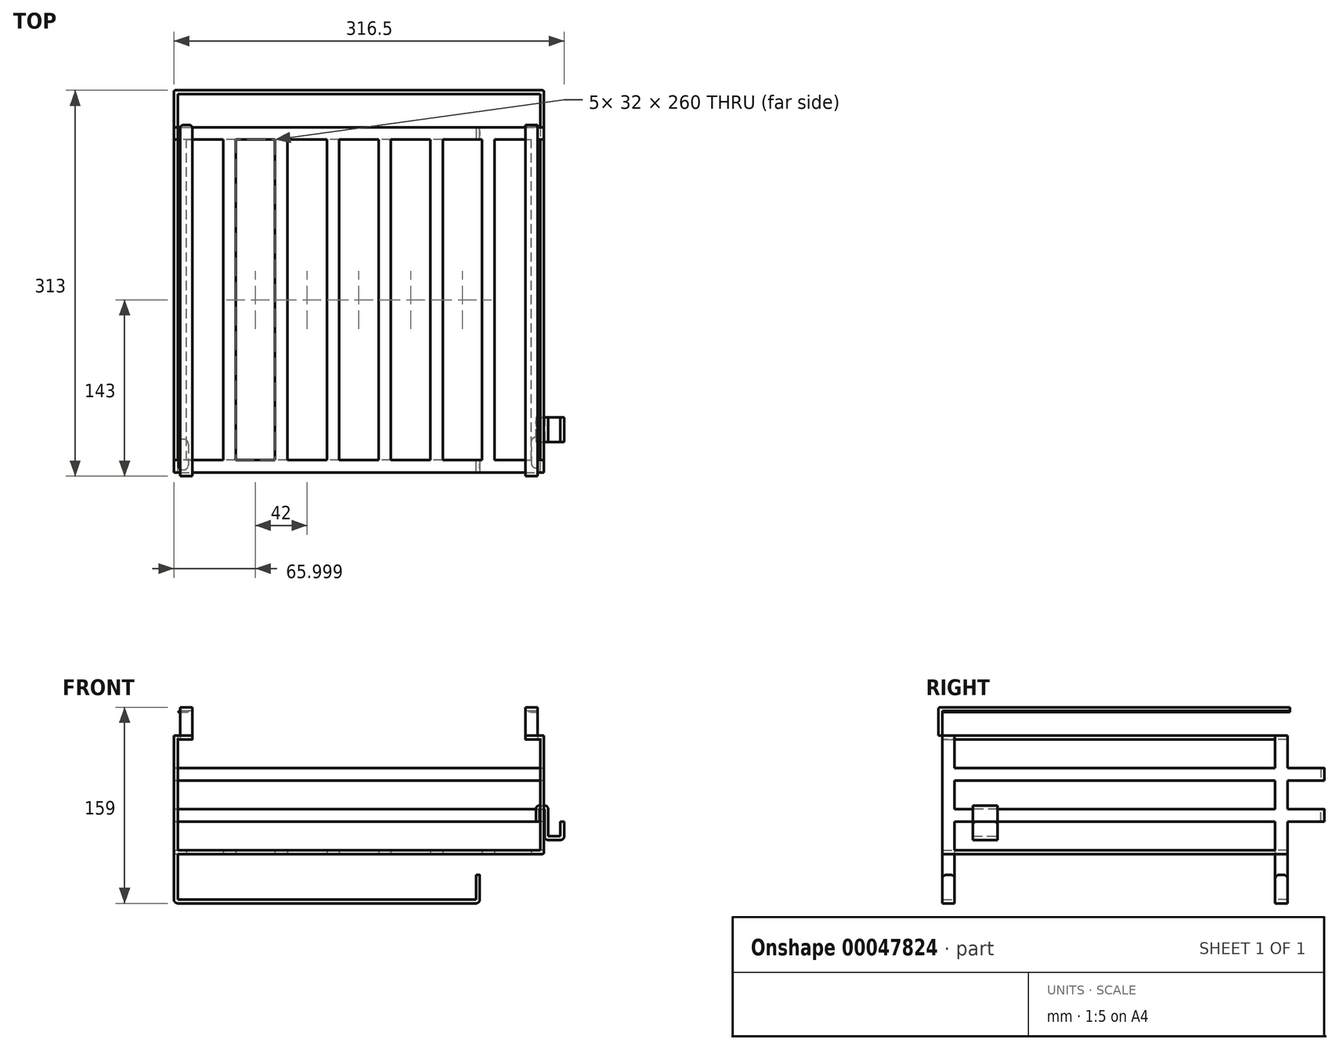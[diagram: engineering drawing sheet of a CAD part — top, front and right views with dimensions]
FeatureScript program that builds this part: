
annotation { "Feature Type Name" : "Feature", "Feature Type Description" : "" }
export const myFeature = defineFeature(function(context is Context, id is Id, definition is map)
    precondition{}
    {
        {
            var Q0;
            Q0=qCreatedBy(makeId("Top.planeOp"),FACE);
            var sketch = newSketch(context, id + "F0", { "sketchPlane" : qUnion([Q0])});
            skLineSegment(sketch, "E0.bottom", {"start": v(-155.28, 215.65) * mm, "end": v(144.72, 215.65) * mm});
            skLineSegment(sketch, "E0.top", {"start": v(-155.28, -94.35) * mm, "end": v(144.72, -94.35) * mm});
            skLineSegment(sketch, "E0.left", {"start": v(-155.28, 215.65) * mm, "end": v(-155.28, -94.35) * mm});
            skLineSegment(sketch, "E0.right", {"start": v(144.72, 215.65) * mm, "end": v(144.72, -94.35) * mm});
            skLineSegment(sketch, "E1", {"start": v(-155.28, -84.35) * mm, "end": v(144.72, -84.35) * mm});
            skLineSegment(sketch, "E2", {"start": v(-115.28, -84.35) * mm, "end": v(-115.28, 175.65) * mm});
            skLineSegment(sketch, "E3.0", {"start": v(-105.28, -84.35) * mm, "end": v(-105.28, 175.65) * mm});
            skLineSegment(sketch, "E4", {"start": v(-73.28, -84.35) * mm, "end": v(-73.28, 175.65) * mm});
            skLineSegment(sketch, "E5.0", {"start": v(-63.28, -84.35) * mm, "end": v(-63.28, 175.65) * mm});
            skLineSegment(sketch, "E6.0", {"start": v(-31.28, -84.35) * mm, "end": v(-31.28, 175.65) * mm});
            skLineSegment(sketch, "E7.0", {"start": v(-21.28, -84.35) * mm, "end": v(-21.28, 175.65) * mm});
            skLineSegment(sketch, "E8.0", {"start": v(10.72, -84.35) * mm, "end": v(10.72, 175.65) * mm});
            skLineSegment(sketch, "E9.0", {"start": v(20.72, -84.35) * mm, "end": v(20.72, 175.65) * mm});
            skLineSegment(sketch, "E10.0", {"start": v(52.72, -84.35) * mm, "end": v(52.72, 175.65) * mm});
            skLineSegment(sketch, "E11.0", {"start": v(62.72, -84.35) * mm, "end": v(62.72, 175.65) * mm});
            skLineSegment(sketch, "E12.0", {"start": v(94.72, -84.35) * mm, "end": v(94.72, 175.65) * mm});
            skLineSegment(sketch, "E13.0", {"start": v(104.72, -84.35) * mm, "end": v(104.72, 175.65) * mm});
            skLineSegment(sketch, "E14", {"start": v(-115.28, -42.82) * mm, "end": v(-155.28, -42.82) * mm, "construction": true});
            skLineSegment(sketch, "E15", {"start": v(104.72, -42.82) * mm, "end": v(144.72, -42.82) * mm, "construction": true});
            skLineSegment(sketch, "E16", {"start": v(-155.28, 175.65) * mm, "end": v(144.72, 175.65) * mm});
            skLineSegment(sketch, "E17.0", {"start": v(-155.28, 185.65) * mm, "end": v(144.72, 185.65) * mm});
            skLineSegment(sketch, "E18", {"start": v(-145.28, -84.35) * mm, "end": v(-145.28, 175.65) * mm});
            skLineSegment(sketch, "E19", {"start": v(134.72, -84.35) * mm, "end": v(134.72, 175.65) * mm});
            skSolve(sketch);
        }
        {
            var Q0;
            {var subQ13=sQuery(id+"F0.wireOp",EDGE,"E17.0");Q0=makeQuery(id+"F0.imprint","IMPRINT",FACE,{"disambiguationData":[TD([[makeQuery(id+"F0.imprint","IMPRINT",EDGE,{"derivedFrom":subQ13}),-1.0]])]});}
            var Q1;
            {var subQ2=sQuery(id+"F0.wireOp",EDGE,"E2");Q1=makeQuery(id+"F0.imprint","IMPRINT",FACE,{"disambiguationData":[TD([[makeQuery(id+"F0.imprint","IMPRINT",EDGE,{"derivedFrom":subQ2}),-1.0]])]});}
            var Q2;
            {var subQ2=sQuery(id+"F0.wireOp",EDGE,"E4");Q2=makeQuery(id+"F0.imprint","IMPRINT",FACE,{"disambiguationData":[TD([[makeQuery(id+"F0.imprint","IMPRINT",EDGE,{"derivedFrom":subQ2}),-1.0]])]});}
            var Q3;
            {var subQ2=sQuery(id+"F0.wireOp",EDGE,"E6.0");Q3=makeQuery(id+"F0.imprint","IMPRINT",FACE,{"disambiguationData":[TD([[makeQuery(id+"F0.imprint","IMPRINT",EDGE,{"derivedFrom":subQ2}),-1.0]])]});}
            var Q4;
            {var subQ2=sQuery(id+"F0.wireOp",EDGE,"E8.0");Q4=makeQuery(id+"F0.imprint","IMPRINT",FACE,{"disambiguationData":[TD([[makeQuery(id+"F0.imprint","IMPRINT",EDGE,{"derivedFrom":subQ2}),-1.0]])]});}
            var Q5;
            {var subQ2=sQuery(id+"F0.wireOp",EDGE,"E10.0");Q5=makeQuery(id+"F0.imprint","IMPRINT",FACE,{"disambiguationData":[TD([[makeQuery(id+"F0.imprint","IMPRINT",EDGE,{"derivedFrom":subQ2}),-1.0]])]});}
            var Q6;
            {var subQ2=sQuery(id+"F0.wireOp",EDGE,"E12.0");Q6=makeQuery(id+"F0.imprint","IMPRINT",FACE,{"disambiguationData":[TD([[makeQuery(id+"F0.imprint","IMPRINT",EDGE,{"derivedFrom":subQ2}),-1.0]])]});}
            var Q7;
            {var subQ6=sQuery(id+"F0.wireOp",EDGE,"E0.top");Q7=makeQuery(id+"F0.imprint","IMPRINT",FACE,{"disambiguationData":[TD([[makeQuery(id+"F0.imprint","IMPRINT",EDGE,{"derivedFrom":subQ6}),1.0]])]});}
            var Q8;
            {var subQ0=sQuery(id+"F0.wireOp",EDGE,"E18");Q8=makeQuery(id+"F0.imprint","IMPRINT",FACE,{"disambiguationData":[TD([[makeQuery(id+"F0.imprint","IMPRINT",EDGE,{"derivedFrom":subQ0}),1.0]])]});}
            var Q9;
            {var subQ0=sQuery(id+"F0.wireOp",EDGE,"E19");Q9=makeQuery(id+"F0.imprint","IMPRINT",FACE,{"disambiguationData":[TD([[makeQuery(id+"F0.imprint","IMPRINT",EDGE,{"derivedFrom":subQ0}),-1.0]])]});}
            extrude(context, id + "F1", {"entities" : qUnion([Q0, Q1, Q2, Q3, Q4, Q5, Q6, Q7, Q8, Q9]), "depth" : 3 * mm});
        }
        {
            var Q0;
            Q0=makeQuery(id+"F1.opExtrude","CAP_FACE",FACE,{"disambiguationData":[OSD([sQuery(id+"F0.wireOp",EDGE,"E0.top"),sQuery(id+"F0.wireOp",EDGE,"E0.left"),sQuery(id+"F0.wireOp",EDGE,"E0.right"),sQuery(id+"F0.wireOp",EDGE,"E1"),sQuery(id+"F0.wireOp",EDGE,"E2"),sQuery(id+"F0.wireOp",EDGE,"E3.0"),sQuery(id+"F0.wireOp",EDGE,"E4"),sQuery(id+"F0.wireOp",EDGE,"E5.0"),sQuery(id+"F0.wireOp",EDGE,"E6.0"),sQuery(id+"F0.wireOp",EDGE,"E7.0"),sQuery(id+"F0.wireOp",EDGE,"E8.0"),sQuery(id+"F0.wireOp",EDGE,"E9.0"),sQuery(id+"F0.wireOp",EDGE,"E10.0"),sQuery(id+"F0.wireOp",EDGE,"E11.0"),sQuery(id+"F0.wireOp",EDGE,"E12.0"),sQuery(id+"F0.wireOp",EDGE,"E13.0"),sQuery(id+"F0.wireOp",EDGE,"E16"),sQuery(id+"F0.wireOp",EDGE,"E17.0")])],"isStart":false});
            var sketch = newSketch(context, id + "F2", { "sketchPlane" : qUnion([Q0])});
            skLineSegment(sketch, "E20.bottom", {"start": v(-155.28, 185.65) * mm, "end": v(-152.28, 185.65) * mm});
            skLineSegment(sketch, "E20.top", {"start": v(-155.28, 175.65) * mm, "end": v(-152.28, 175.65) * mm});
            skLineSegment(sketch, "E20.left", {"start": v(-155.28, 185.65) * mm, "end": v(-155.28, 175.65) * mm});
            skLineSegment(sketch, "E20.right", {"start": v(-152.28, 185.65) * mm, "end": v(-152.28, 175.65) * mm});
            skLineSegment(sketch, "E21.bottom", {"start": v(-155.28, -94.35) * mm, "end": v(-152.28, -94.35) * mm});
            skLineSegment(sketch, "E21.top", {"start": v(-155.28, -84.35) * mm, "end": v(-152.28, -84.35) * mm});
            skLineSegment(sketch, "E21.left", {"start": v(-155.28, -94.35) * mm, "end": v(-155.28, -84.35) * mm});
            skLineSegment(sketch, "E21.right", {"start": v(-152.28, -94.35) * mm, "end": v(-152.28, -84.35) * mm});
            skLineSegment(sketch, "E22", {"start": v(-5.28, 152.07) * mm, "end": v(-5.28, 185.65) * mm, "construction": true});
            skLineSegment(sketch, "E23.MirrorCS", {"start": v(141.72, 185.65) * mm, "end": v(141.72, 175.65) * mm});
            skLineSegment(sketch, "E24.MirrorCS", {"start": v(144.72, 185.65) * mm, "end": v(144.72, 175.65) * mm});
            skLineSegment(sketch, "E25.MirrorCS", {"start": v(144.72, 185.65) * mm, "end": v(141.72, 185.65) * mm});
            skLineSegment(sketch, "E26.MirrorCS", {"start": v(144.72, 175.65) * mm, "end": v(141.72, 175.65) * mm});
            skLineSegment(sketch, "E27.MirrorCS", {"start": v(141.72, -94.35) * mm, "end": v(141.72, -84.35) * mm});
            skLineSegment(sketch, "E28.MirrorCS", {"start": v(144.72, -94.35) * mm, "end": v(144.72, -84.35) * mm});
            skLineSegment(sketch, "E29.MirrorCS", {"start": v(144.72, -84.35) * mm, "end": v(141.72, -84.35) * mm});
            skLineSegment(sketch, "E30.MirrorCS", {"start": v(144.72, -94.35) * mm, "end": v(141.72, -94.35) * mm});
            skSolve(sketch);
        }
        {
            var Q0;
            Q0=makeQuery(id+"F2.imprint","IMPRINT",FACE,{"disambiguationData":[TD([[makeQuery(id+"F2.imprint","IMPRINT",EDGE,{"derivedFrom":sQuery(id+"F2.wireOp",EDGE,"E20.bottom")}),-1.0]])]});
            var Q1;
            Q1=makeQuery(id+"F2.imprint","IMPRINT",FACE,{"disambiguationData":[TD([[makeQuery(id+"F2.imprint","IMPRINT",EDGE,{"derivedFrom":sQuery(id+"F2.wireOp",EDGE,"E23.MirrorCS")}),1.0]])]});
            var Q2;
            Q2=makeQuery(id+"F2.imprint","IMPRINT",FACE,{"disambiguationData":[TD([[makeQuery(id+"F2.imprint","IMPRINT",EDGE,{"derivedFrom":sQuery(id+"F2.wireOp",EDGE,"E27.MirrorCS")}),-1.0]])]});
            var Q3;
            Q3=makeQuery(id+"F2.imprint","IMPRINT",FACE,{"disambiguationData":[TD([[makeQuery(id+"F2.imprint","IMPRINT",EDGE,{"derivedFrom":sQuery(id+"F2.wireOp",EDGE,"E21.bottom")}),1.0]])]});
            extrude(context, id + "F3", {"entities" : qUnion([Q0, Q1, Q2, Q3]), "operationType" : NewBodyOperationType.ADD, "depth" : 90 * mm});
        }
        {
            var Q0;
            Q0=makeQuery(id+"F3.opExtrude","CAP_FACE",FACE,{"disambiguationData":[OSD([sQuery(id+"F2.wireOp",EDGE,"E20.bottom"),sQuery(id+"F2.wireOp",EDGE,"E20.top"),sQuery(id+"F2.wireOp",EDGE,"E20.left"),sQuery(id+"F2.wireOp",EDGE,"E20.right")])],"isStart":false});
            var sketch = newSketch(context, id + "F4", { "sketchPlane" : qUnion([Q0])});
            skLineSegment(sketch, "E31.bottom", {"start": v(-150.28, 185.65) * mm, "end": v(-140.28, 185.65) * mm});
            skLineSegment(sketch, "E31.top", {"start": v(-150.28, -94.35) * mm, "end": v(-140.28, -94.35) * mm});
            skLineSegment(sketch, "E31.left", {"start": v(-150.28, 185.65) * mm, "end": v(-150.28, -94.35) * mm});
            skLineSegment(sketch, "E31.right", {"start": v(-140.28, 185.65) * mm, "end": v(-140.28, -94.35) * mm});
            skLineSegment(sketch, "E32.MirrorCS", {"start": v(129.72, 185.65) * mm, "end": v(129.72, -94.35) * mm});
            skLineSegment(sketch, "E33.MirrorCS", {"start": v(139.72, 185.65) * mm, "end": v(139.72, -94.35) * mm});
            skLineSegment(sketch, "E34.MirrorCS", {"start": v(139.72, 185.65) * mm, "end": v(129.72, 185.65) * mm});
            skLineSegment(sketch, "E35.MirrorCS", {"start": v(139.72, -94.35) * mm, "end": v(129.72, -94.35) * mm});
            skLineSegment(sketch, "E36.bottom", {"start": v(-150.28, -94.35) * mm, "end": v(-155.28, -94.35) * mm});
            skLineSegment(sketch, "E36.top", {"start": v(-150.28, -84.35) * mm, "end": v(-155.28, -84.35) * mm});
            skLineSegment(sketch, "E36.left", {"start": v(-150.28, -94.35) * mm, "end": v(-150.28, -84.35) * mm});
            skLineSegment(sketch, "E36.right", {"start": v(-155.28, -94.35) * mm, "end": v(-155.28, -84.35) * mm});
            skLineSegment(sketch, "E37.MirrorCS", {"start": v(139.72, -84.35) * mm, "end": v(144.72, -84.35) * mm});
            skLineSegment(sketch, "E38.MirrorCS", {"start": v(144.72, -94.35) * mm, "end": v(144.72, -84.35) * mm});
            skLineSegment(sketch, "E39.MirrorCS", {"start": v(139.72, -94.35) * mm, "end": v(144.72, -94.35) * mm});
            skLineSegment(sketch, "E40.bottom", {"start": v(-150.28, 185.65) * mm, "end": v(-155.28, 185.65) * mm});
            skLineSegment(sketch, "E40.top", {"start": v(-150.28, 175.65) * mm, "end": v(-155.28, 175.65) * mm});
            skLineSegment(sketch, "E40.left", {"start": v(-150.28, 185.65) * mm, "end": v(-150.28, 175.65) * mm});
            skLineSegment(sketch, "E40.right", {"start": v(-155.28, 185.65) * mm, "end": v(-155.28, 175.65) * mm});
            skLineSegment(sketch, "E41.MirrorCS", {"start": v(139.72, 175.65) * mm, "end": v(144.72, 175.65) * mm});
            skLineSegment(sketch, "E42.MirrorCS", {"start": v(139.72, 185.65) * mm, "end": v(144.72, 185.65) * mm});
            skLineSegment(sketch, "E43.MirrorCS", {"start": v(144.72, 185.65) * mm, "end": v(144.72, 175.65) * mm});
            skLineSegment(sketch, "E44.bottom", {"start": v(-140.28, -94.35) * mm, "end": v(-150.28, -94.35) * mm});
            skLineSegment(sketch, "E44.top", {"start": v(-140.28, -97.35) * mm, "end": v(-150.28, -97.35) * mm});
            skLineSegment(sketch, "E44.left", {"start": v(-140.28, -94.35) * mm, "end": v(-140.28, -97.35) * mm});
            skLineSegment(sketch, "E44.right", {"start": v(-150.28, -94.35) * mm, "end": v(-150.28, -97.35) * mm});
            skLineSegment(sketch, "E45.top", {"start": v(139.72, -97.35) * mm, "end": v(129.72, -97.35) * mm});
            skLineSegment(sketch, "E45.left", {"start": v(139.72, -94.35) * mm, "end": v(139.72, -97.35) * mm});
            skLineSegment(sketch, "E45.right", {"start": v(129.72, -94.35) * mm, "end": v(129.72, -97.35) * mm});
            skSolve(sketch);
        }
        {
            var Q0;
            Q0=makeQuery(id+"F4.imprint","IMPRINT",FACE,{"disambiguationData":[TD([[makeQuery(id+"F4.imprint","IMPRINT",EDGE,{"derivedFrom":sQuery(id+"F4.wireOp",EDGE,"E31.bottom")}),-1.0]])]});
            var Q1;
            {var subQ1=sQuery(id+"F4.wireOp",EDGE,"E40.left");Q1=makeQuery(id+"F4.imprint","IMPRINT",FACE,{"disambiguationData":[TD([[makeQuery(id+"F4.imprint","IMPRINT",EDGE,{"derivedFrom":subQ1}),-1.0]])]});}
            var Q2;
            {var subQ1=sQuery(id+"F4.wireOp",EDGE,"E40.right");Q2=makeQuery(id+"F4.imprint","IMPRINT",FACE,{"disambiguationData":[TD([[makeQuery(id+"F4.imprint","IMPRINT",EDGE,{"derivedFrom":subQ1}),1.0]])]});}
            var Q3;
            Q3=makeQuery(id+"F4.imprint","IMPRINT",FACE,{"disambiguationData":[TD([[makeQuery(id+"F4.imprint","IMPRINT",EDGE,{"derivedFrom":sQuery(id+"F4.wireOp",EDGE,"E44.bottom")}),1.0]])]});
            var Q4;
            Q4=makeQuery(id+"F4.imprint","IMPRINT",FACE,{"disambiguationData":[TD([[makeQuery(id+"F4.imprint","IMPRINT",EDGE,{"derivedFrom":sQuery(id+"F4.wireOp",EDGE,"E35.MirrorCS")}),1.0]])]});
            var Q5;
            Q5=makeQuery(id+"F4.imprint","IMPRINT",FACE,{"disambiguationData":[TD([[makeQuery(id+"F4.imprint","IMPRINT",EDGE,{"derivedFrom":sQuery(id+"F4.wireOp",EDGE,"E32.MirrorCS")}),1.0]])]});
            var Q6;
            {var subQ1=sQuery(id+"F4.wireOp",EDGE,"E37.MirrorCS");Q6=makeQuery(id+"F4.imprint","IMPRINT",FACE,{"disambiguationData":[TD([[makeQuery(id+"F4.imprint","IMPRINT",EDGE,{"derivedFrom":subQ1}),-1.0]])]});}
            var Q7;
            {var subQ1=sQuery(id+"F4.wireOp",EDGE,"E41.MirrorCS");Q7=makeQuery(id+"F4.imprint","IMPRINT",FACE,{"disambiguationData":[TD([[makeQuery(id+"F4.imprint","IMPRINT",EDGE,{"derivedFrom":subQ1}),1.0]])]});}
            var Q8;
            Q8=makeQuery(id+"F4.imprint","IMPRINT",FACE,{"disambiguationData":[TD([[makeQuery(id+"F4.imprint","IMPRINT",EDGE,{"derivedFrom":sQuery(id+"F4.wireOp",EDGE,"E36.bottom")}),-1.0]])]});
            extrude(context, id + "F5", {"entities" : qUnion([Q0, Q1, Q2, Q3, Q4, Q5, Q6, Q7, Q8]), "operationType" : NewBodyOperationType.ADD, "depth" : 3 * mm});
        }
        {
            var Q0;
            Q0=makeQuery(id+"F5.opExtrude","CAP_FACE",FACE,{"disambiguationData":[OSD([sQuery(id+"F4.wireOp",EDGE,"E31.bottom"),sQuery(id+"F4.wireOp",EDGE,"E31.top"),sQuery(id+"F4.wireOp",EDGE,"E31.left"),sQuery(id+"F4.wireOp",EDGE,"E31.right")])],"isStart":false});
            var sketch = newSketch(context, id + "F6", { "sketchPlane" : qUnion([Q0])});
            skLineSegment(sketch, "E46.bottom", {"start": v(-140.28, -97.35) * mm, "end": v(-150.28, -97.35) * mm});
            skLineSegment(sketch, "E46.top", {"start": v(-140.28, -94.35) * mm, "end": v(-150.28, -94.35) * mm});
            skLineSegment(sketch, "E46.left", {"start": v(-140.28, -97.35) * mm, "end": v(-140.28, -94.35) * mm});
            skLineSegment(sketch, "E46.right", {"start": v(-150.28, -97.35) * mm, "end": v(-150.28, -94.35) * mm});
            skLineSegment(sketch, "E47.MirrorCS", {"start": v(129.72, -94.35) * mm, "end": v(139.72, -94.35) * mm});
            skLineSegment(sketch, "E48.MirrorCS", {"start": v(139.72, -97.35) * mm, "end": v(139.72, -94.35) * mm});
            skLineSegment(sketch, "E49.MirrorCS", {"start": v(129.72, -97.35) * mm, "end": v(129.72, -94.35) * mm});
            skLineSegment(sketch, "E50.MirrorCS", {"start": v(129.72, -97.35) * mm, "end": v(139.72, -97.35) * mm});
            skSolve(sketch);
        }
        {
            var Q0;
            Q0=makeQuery(id+"F6.imprint","IMPRINT",FACE,{"disambiguationData":[TD([[makeQuery(id+"F6.imprint","IMPRINT",EDGE,{"derivedFrom":sQuery(id+"F6.wireOp",EDGE,"E46.bottom")}),-1.0]])]});
            var Q1;
            Q1=makeQuery(id+"F6.imprint","IMPRINT",FACE,{"disambiguationData":[TD([[makeQuery(id+"F6.imprint","IMPRINT",EDGE,{"derivedFrom":sQuery(id+"F6.wireOp",EDGE,"E47.MirrorCS")}),-1.0]])]});
            extrude(context, id + "F7", {"entities" : qUnion([Q0, Q1]), "operationType" : NewBodyOperationType.ADD, "depth" : 20 * mm});
        }
        {
            var Q0;
            Q0=makeQuery(id+"F7.opExtrude","CAP_FACE",FACE,{"disambiguationData":[OSD([sQuery(id+"F6.wireOp",EDGE,"E46.bottom"),sQuery(id+"F6.wireOp",EDGE,"E46.top"),sQuery(id+"F6.wireOp",EDGE,"E46.left"),sQuery(id+"F6.wireOp",EDGE,"E46.right")])],"isStart":false});
            var sketch = newSketch(context, id + "F8", { "sketchPlane" : qUnion([Q0])});
            skLineSegment(sketch, "E51.bottom", {"start": v(-150.28, -97.35) * mm, "end": v(-140.28, -97.35) * mm});
            skLineSegment(sketch, "E51.top", {"start": v(-150.28, 187.65) * mm, "end": v(-140.28, 187.65) * mm});
            skLineSegment(sketch, "E51.left", {"start": v(-150.28, -97.35) * mm, "end": v(-150.28, 187.65) * mm});
            skLineSegment(sketch, "E51.right", {"start": v(-140.28, -97.35) * mm, "end": v(-140.28, 187.65) * mm});
            skLineSegment(sketch, "E52.MirrorCS", {"start": v(129.72, -97.35) * mm, "end": v(129.72, 187.65) * mm});
            skLineSegment(sketch, "E53.MirrorCS", {"start": v(139.72, 187.65) * mm, "end": v(129.72, 187.65) * mm});
            skLineSegment(sketch, "E54.MirrorCS", {"start": v(139.72, -97.35) * mm, "end": v(139.72, 187.65) * mm});
            skLineSegment(sketch, "E55.MirrorCS", {"start": v(139.72, -97.35) * mm, "end": v(129.72, -97.35) * mm});
            skPoint(sketch, "E56", {"position": v(-140.28, 45.15) * mm});
            skSolve(sketch);
        }
        {
            var Q0;
            {var subQ1=sQuery(id+"F8.wireOp",EDGE,"E51.top");Q0=makeQuery(id+"F8.imprint","IMPRINT",FACE,{"disambiguationData":[TD([[makeQuery(id+"F8.imprint","IMPRINT",EDGE,{"derivedFrom":subQ1}),-1.0]])]});}
            var Q1;
            Q1=makeQuery(id+"F8.imprint","IMPRINT",FACE,{"disambiguationData":[TD([[makeQuery(id+"F8.imprint","IMPRINT",EDGE,{"derivedFrom":sQuery(id+"F8.wireOp",EDGE,"E52.MirrorCS")}),-1.0]])]});
            var Q2;
            {var subQ2=sQuery(id+"F8.wireOp",EDGE,"E51.bottom");Q2=makeQuery(id+"F8.imprint","IMPRINT",FACE,{"disambiguationData":[TD([[makeQuery(id+"F8.imprint","IMPRINT",EDGE,{"derivedFrom":subQ2}),1.0]])]});}
            var Q3;
            {var subQ2=sQuery(id+"F8.wireOp",EDGE,"E51.bottom");Q3=makeQuery(id+"F8.imprint","IMPRINT",FACE,{"disambiguationData":[TD([[makeQuery(id+"F8.imprint","IMPRINT",EDGE,{"derivedFrom":subQ2}),-1.0]])]});}
            extrude(context, id + "F9", {"entities" : qUnion([Q0, Q1, Q2, Q3]), "operationType" : NewBodyOperationType.ADD, "depth" : 3 * mm});
        }
        {
            var Q0;
            Q0=makeQuery(id+"F5.boolean.opBoolean","MERGE",FACE,{"derivedFrom":[makeQuery(id+"F3.boolean.opBoolean","MERGE",FACE,{"derivedFrom":[makeQuery(id+"F1.opExtrude","SWEPT_FACE",FACE,{"disambiguationData":[OSD([sQuery(id+"F0.wireOp",EDGE,"E17.0")])]}),makeQuery(id+"F3.opExtrude","SWEPT_FACE",FACE,{"disambiguationData":[OSD([sQuery(id+"F2.wireOp",EDGE,"E20.bottom")])]}),makeQuery(id+"F3.opExtrude","SWEPT_FACE",FACE,{"disambiguationData":[OSD([sQuery(id+"F2.wireOp",EDGE,"E25.MirrorCS")])]})]}),makeQuery(id+"F5.opExtrude","SWEPT_FACE",FACE,{"disambiguationData":[OSD([sQuery(id+"F4.wireOp",EDGE,"E31.bottom")])]}),makeQuery(id+"F5.opExtrude","SWEPT_FACE",FACE,{"disambiguationData":[OSD([sQuery(id+"F4.wireOp",EDGE,"E34.MirrorCS")])]})]});
            var sketch = newSketch(context, id + "F10", { "sketchPlane" : qUnion([Q0])});
            skLineSegment(sketch, "E57", {"start": v(152.28, 3) * mm, "end": v(155.28, 3) * mm, "construction": true});
            skLineSegment(sketch, "E58", {"start": v(152.28, 93) * mm, "end": v(155.28, 93) * mm, "construction": true});
            skLineSegment(sketch, "E59.bottom", {"start": v(155.28, 69.67) * mm, "end": v(152.28, 69.67) * mm});
            skLineSegment(sketch, "E59.top", {"start": v(155.28, 59.67) * mm, "end": v(152.28, 59.67) * mm});
            skLineSegment(sketch, "E59.left", {"start": v(155.28, 69.67) * mm, "end": v(155.28, 59.67) * mm});
            skLineSegment(sketch, "E59.right", {"start": v(152.28, 69.67) * mm, "end": v(152.28, 59.67) * mm});
            skLineSegment(sketch, "E60.bottom", {"start": v(155.28, 36.33) * mm, "end": v(152.28, 36.33) * mm});
            skLineSegment(sketch, "E60.top", {"start": v(155.28, 26.33) * mm, "end": v(152.28, 26.33) * mm});
            skLineSegment(sketch, "E60.left", {"start": v(155.28, 36.33) * mm, "end": v(155.28, 26.33) * mm});
            skLineSegment(sketch, "E60.right", {"start": v(152.28, 36.33) * mm, "end": v(152.28, 26.33) * mm});
            skLineSegment(sketch, "E61", {"start": v(153.78, 93) * mm, "end": v(153.78, 69.67) * mm, "construction": true});
            skLineSegment(sketch, "E62", {"start": v(153.78, 59.67) * mm, "end": v(153.78, 36.33) * mm, "construction": true});
            skLineSegment(sketch, "E63", {"start": v(153.78, 26.33) * mm, "end": v(153.78, 3) * mm, "construction": true});
            skLineSegment(sketch, "E64", {"start": v(5.28, 3) * mm, "end": v(5.28, 25.42) * mm, "construction": true});
            skLineSegment(sketch, "E65.MirrorCS", {"start": v(-144.72, 26.33) * mm, "end": v(-141.72, 26.33) * mm});
            skLineSegment(sketch, "E66.MirrorCS", {"start": v(-144.72, 36.33) * mm, "end": v(-141.72, 36.33) * mm});
            skLineSegment(sketch, "E67.MirrorCS", {"start": v(-141.72, 36.33) * mm, "end": v(-141.72, 26.33) * mm});
            skLineSegment(sketch, "E68.MirrorCS", {"start": v(-144.72, 36.33) * mm, "end": v(-144.72, 26.33) * mm});
            skLineSegment(sketch, "E69.MirrorCS", {"start": v(-144.72, 59.67) * mm, "end": v(-141.72, 59.67) * mm});
            skLineSegment(sketch, "E70.MirrorCS", {"start": v(-141.72, 69.67) * mm, "end": v(-141.72, 59.67) * mm});
            skLineSegment(sketch, "E71.MirrorCS", {"start": v(-144.72, 69.67) * mm, "end": v(-144.72, 59.67) * mm});
            skLineSegment(sketch, "E72.MirrorCS", {"start": v(-144.72, 69.67) * mm, "end": v(-141.72, 69.67) * mm});
            skSolve(sketch);
        }
        {
            var Q0;
            Q0=makeQuery(id+"F10.imprint","IMPRINT",FACE,{"disambiguationData":[TD([[makeQuery(id+"F10.imprint","IMPRINT",EDGE,{"derivedFrom":sQuery(id+"F10.wireOp",EDGE,"E59.bottom")}),1.0]])]});
            var Q1;
            Q1=makeQuery(id+"F10.imprint","IMPRINT",FACE,{"disambiguationData":[TD([[makeQuery(id+"F10.imprint","IMPRINT",EDGE,{"derivedFrom":sQuery(id+"F10.wireOp",EDGE,"E60.bottom")}),1.0]])]});
            var Q2;
            Q2=makeQuery(id+"F10.imprint","IMPRINT",FACE,{"disambiguationData":[TD([[makeQuery(id+"F10.imprint","IMPRINT",EDGE,{"derivedFrom":sQuery(id+"F10.wireOp",EDGE,"E69.MirrorCS")}),1.0]])]});
            var Q3;
            Q3=makeQuery(id+"F10.imprint","IMPRINT",FACE,{"disambiguationData":[TD([[makeQuery(id+"F10.imprint","IMPRINT",EDGE,{"derivedFrom":sQuery(id+"F10.wireOp",EDGE,"E65.MirrorCS")}),1.0]])]});
            var Q4;
            Q4=makeQuery(id+"F5.boolean.opBoolean","MERGE",FACE,{"derivedFrom":[makeQuery(id+"F3.opExtrude","SWEPT_FACE",FACE,{"disambiguationData":[OSD([sQuery(id+"F2.wireOp",EDGE,"E21.top")])]}),makeQuery(id+"F5.opExtrude","SWEPT_FACE",FACE,{"disambiguationData":[OSD([sQuery(id+"F4.wireOp",EDGE,"E36.top")])]})]});
            extrude(context, id + "F11", {"entities" : qUnion([Q0, Q1, Q2, Q3]), "operationType" : NewBodyOperationType.ADD, "depth" : 30 * mm, "hasSecondDirection" : true, "secondDirectionBound" : SecondDirectionBoundingType.UP_TO_SURFACE, "secondDirectionOppositeDirection" : true, "secondDirectionBoundEntityFace" : qUnion([Q4]), "secondDirectionDepth" : 25 * mm});
        }
        {
            var Q0;
            Q0=makeQuery(id+"F11.boolean.opBoolean","MERGE",FACE,{"derivedFrom":[makeQuery(id+"F3.opExtrude","SWEPT_FACE",FACE,{"disambiguationData":[OSD([sQuery(id+"F2.wireOp",EDGE,"E20.right")])]}),makeQuery(id+"F3.opExtrude","SWEPT_FACE",FACE,{"disambiguationData":[OSD([sQuery(id+"F2.wireOp",EDGE,"E21.right")])]}),makeQuery(id+"F11.opExtrude","SWEPT_FACE",FACE,{"disambiguationData":[OSD([sQuery(id+"F10.wireOp",EDGE,"E59.right")])]}),makeQuery(id+"F11.opExtrude","SWEPT_FACE",FACE,{"disambiguationData":[OSD([sQuery(id+"F10.wireOp",EDGE,"E60.right")])]})]});
            var sketch = newSketch(context, id + "F12", { "sketchPlane" : qUnion([Q0])});
            skLineSegment(sketch, "E73.bottom", {"start": v(215.65, 69.67) * mm, "end": v(212.65, 69.67) * mm});
            skLineSegment(sketch, "E73.top", {"start": v(215.65, 59.67) * mm, "end": v(212.65, 59.67) * mm});
            skLineSegment(sketch, "E73.left", {"start": v(215.65, 69.67) * mm, "end": v(215.65, 59.67) * mm});
            skLineSegment(sketch, "E73.right", {"start": v(212.65, 69.67) * mm, "end": v(212.65, 59.67) * mm});
            skLineSegment(sketch, "E74.bottom", {"start": v(215.65, 26.33) * mm, "end": v(212.65, 26.33) * mm});
            skLineSegment(sketch, "E74.top", {"start": v(215.65, 36.33) * mm, "end": v(212.65, 36.33) * mm});
            skLineSegment(sketch, "E74.left", {"start": v(215.65, 26.33) * mm, "end": v(215.65, 36.33) * mm});
            skLineSegment(sketch, "E74.right", {"start": v(212.65, 26.33) * mm, "end": v(212.65, 36.33) * mm});
            skSolve(sketch);
        }
        {
            var Q0;
            Q0=makeQuery(id+"F12.imprint","IMPRINT",FACE,{"disambiguationData":[TD([[makeQuery(id+"F12.imprint","IMPRINT",EDGE,{"derivedFrom":sQuery(id+"F12.wireOp",EDGE,"E73.bottom")}),1.0]])]});
            var Q1;
            Q1=makeQuery(id+"F12.imprint","IMPRINT",FACE,{"disambiguationData":[TD([[makeQuery(id+"F12.imprint","IMPRINT",EDGE,{"derivedFrom":sQuery(id+"F12.wireOp",EDGE,"E74.bottom")}),-1.0]])]});
            var Q2;
            Q2=makeQuery(id+"F11.boolean.opBoolean","MERGE",FACE,{"derivedFrom":[makeQuery(id+"F3.opExtrude","SWEPT_FACE",FACE,{"disambiguationData":[OSD([sQuery(id+"F2.wireOp",EDGE,"E23.MirrorCS")])]}),makeQuery(id+"F3.opExtrude","SWEPT_FACE",FACE,{"disambiguationData":[OSD([sQuery(id+"F2.wireOp",EDGE,"E27.MirrorCS")])]}),makeQuery(id+"F11.opExtrude","SWEPT_FACE",FACE,{"disambiguationData":[OSD([sQuery(id+"F10.wireOp",EDGE,"E67.MirrorCS")])]}),makeQuery(id+"F11.opExtrude","SWEPT_FACE",FACE,{"disambiguationData":[OSD([sQuery(id+"F10.wireOp",EDGE,"E70.MirrorCS")])]})]});
            extrude(context, id + "F13", {"entities" : qUnion([Q0, Q1]), "operationType" : NewBodyOperationType.ADD, "endBound" : BoundingType.UP_TO_SURFACE, "endBoundEntityFace" : qUnion([Q2]), "depth" : 25 * mm});
        }
        {
            var Q0;
            {var subQ0=sQuery(id+"F0.wireOp",EDGE,"E0.left");Q0=makeQuery(id+"F1.opExtrude","CAP_EDGE",EDGE,{"disambiguationData":[OSD([subQ0]),TDD([makeQuery(id+"F0.imprint","IMPRINT",EDGE,{"disambiguationData":[TD([[makeQuery(id+"F0.imprint","INTERSECT",VERTEX,{"derivedFrom":[subQ0,sQuery(id+"F0.wireOp",EDGE,"E16")]}),1.0]])],"derivedFrom":subQ0})])],"isStart":true});}
            var Q1;
            {var subQ0=sQuery(id+"F0.wireOp",EDGE,"E0.left");Q1=makeQuery(id+"F1.opExtrude","CAP_EDGE",EDGE,{"disambiguationData":[OSD([subQ0]),TDD([makeQuery(id+"F0.imprint","IMPRINT",EDGE,{"disambiguationData":[TD([[makeQuery(id+"F0.imprint","INTERSECT",VERTEX,{"derivedFrom":[sQuery(id+"F0.wireOp",EDGE,"E0.top"),subQ0]}),1.0]])],"derivedFrom":subQ0})])],"isStart":true});}
            var Q2;
            {var subQ0=sQuery(id+"F0.wireOp",EDGE,"E0.right");Q2=makeQuery(id+"F1.opExtrude","CAP_EDGE",EDGE,{"disambiguationData":[OSD([subQ0]),TDD([makeQuery(id+"F0.imprint","IMPRINT",EDGE,{"disambiguationData":[TD([[makeQuery(id+"F0.imprint","INTERSECT",VERTEX,{"derivedFrom":[sQuery(id+"F0.wireOp",EDGE,"E0.top"),subQ0]}),1.0]])],"derivedFrom":subQ0})])],"isStart":true});}
            var Q3;
            {var subQ0=sQuery(id+"F0.wireOp",EDGE,"E0.right");Q3=makeQuery(id+"F1.opExtrude","CAP_EDGE",EDGE,{"disambiguationData":[OSD([subQ0]),TDD([makeQuery(id+"F0.imprint","IMPRINT",EDGE,{"disambiguationData":[TD([[makeQuery(id+"F0.imprint","INTERSECT",VERTEX,{"derivedFrom":[subQ0,sQuery(id+"F0.wireOp",EDGE,"E16")]}),1.0]])],"derivedFrom":subQ0})])],"isStart":true});}
            var Q4;
            Q4=makeQuery(id+"F11.opExtrude","CAP_EDGE",EDGE,{"disambiguationData":[OSD([sQuery(id+"F10.wireOp",EDGE,"E68.MirrorCS")])],"isStart":false});
            var Q5;
            Q5=makeQuery(id+"F11.opExtrude","CAP_EDGE",EDGE,{"disambiguationData":[OSD([sQuery(id+"F10.wireOp",EDGE,"E71.MirrorCS")])],"isStart":false});
            var Q6;
            Q6=makeQuery(id+"F11.opExtrude","CAP_EDGE",EDGE,{"disambiguationData":[OSD([sQuery(id+"F10.wireOp",EDGE,"E59.left")])],"isStart":false});
            var Q7;
            Q7=makeQuery(id+"F11.opExtrude","CAP_EDGE",EDGE,{"disambiguationData":[OSD([sQuery(id+"F10.wireOp",EDGE,"E60.left")])],"isStart":false});
            var Q8;
            Q8=makeQuery(id+"F5.opExtrude","CAP_EDGE",EDGE,{"disambiguationData":[OSD([sQuery(id+"F4.wireOp",EDGE,"E31.left")])],"isStart":false});
            var Q9;
            Q9=makeQuery(id+"F9.opExtrude","CAP_EDGE",EDGE,{"disambiguationData":[OSD([sQuery(id+"F8.wireOp",EDGE,"E51.bottom")])],"isStart":false});
            var Q10;
            Q10=makeQuery(id+"F9.opExtrude","CAP_EDGE",EDGE,{"disambiguationData":[OSD([sQuery(id+"F8.wireOp",EDGE,"E55.MirrorCS")])],"isStart":false});
            var Q11;
            Q11=makeQuery(id+"F5.opExtrude","CAP_EDGE",EDGE,{"disambiguationData":[OSD([sQuery(id+"F4.wireOp",EDGE,"E33.MirrorCS")])],"isStart":false});
            var Q12;
            Q12=makeQuery(id+"F5.opExtrude","CAP_EDGE",EDGE,{"disambiguationData":[OSD([sQuery(id+"F4.wireOp",EDGE,"E31.top")])],"isStart":true});
            var Q13;
            Q13=makeQuery(id+"F5.opExtrude","CAP_EDGE",EDGE,{"disambiguationData":[OSD([sQuery(id+"F4.wireOp",EDGE,"E35.MirrorCS")])],"isStart":true});
            fillet(context, id + "F14", {"entities" : qUnion([Q0, Q1, Q2, Q3, Q4, Q5, Q6, Q7, Q8, Q9, Q10, Q11, Q12, Q13]), "radius" : 1 * mm, "tangentPropagation" : true, "allowEdgeOverflow" : false});
        }
        {
            var Q0;
            Q0=makeQuery(id+"F9.opExtrude","CAP_FACE",FACE,{"disambiguationData":[OSD([sQuery(id+"F8.wireOp",EDGE,"E52.MirrorCS"),sQuery(id+"F8.wireOp",EDGE,"E53.MirrorCS"),sQuery(id+"F8.wireOp",EDGE,"E54.MirrorCS"),sQuery(id+"F8.wireOp",EDGE,"E55.MirrorCS")])],"isStart":true});
            var sketch = newSketch(context, id + "F15", { "sketchPlane" : qUnion([Q0])});
            skLineSegment(sketch, "E75.bottom", {"start": v(133.1, -163.16) * mm, "end": v(141.1, -163.16) * mm, "construction": true});
            skLineSegment(sketch, "E75.top", {"start": v(133.1, -180.16) * mm, "end": v(141.1, -180.16) * mm, "construction": true});
            skLineSegment(sketch, "E75.left", {"start": v(133.1, -163.16) * mm, "end": v(133.1, -180.16) * mm});
            skLineSegment(sketch, "E75.right", {"start": v(141.1, -163.16) * mm, "end": v(141.1, -180.16) * mm});
            skLineSegment(sketch, "E76", {"start": v(-140.28, -45.15) * mm, "end": v(129.72, -46.65) * mm, "construction": true});
            skLineSegment(sketch, "E77", {"start": v(-5.28, -45.9) * mm, "end": v(-5.34, -56.72) * mm, "construction": true});
            skArc(sketch, "E78", {"start": v(133.1, -180.16) * mm, "mid": v(137.1, -184.16) * mm, "end": v(141.1, -180.16) * mm});
            skArc(sketch, "E79", {"start": v(141.1, -163.16) * mm, "mid": v(137.1, -159.16) * mm, "end": v(133.1, -163.16) * mm});
            skArc(sketch, "E80.MirrorCS", {"start": v(134.58, 86.81) * mm, "mid": v(138.62, 90.77) * mm, "end": v(142.58, 86.72) * mm});
            skLineSegment(sketch, "E81.MirrorCS", {"start": v(134.4, 69.81) * mm, "end": v(134.58, 86.81) * mm});
            skLineSegment(sketch, "E82.MirrorCS", {"start": v(142.39, 69.72) * mm, "end": v(142.58, 86.72) * mm});
            skArc(sketch, "E83.MirrorCS", {"start": v(142.39, 69.72) * mm, "mid": v(138.35, 65.77) * mm, "end": v(134.4, 69.81) * mm});
            skArc(sketch, "E84.MirrorCS", {"start": v(-145.14, -178.61) * mm, "mid": v(-149.19, -182.57) * mm, "end": v(-153.14, -178.52) * mm});
            skLineSegment(sketch, "E85.MirrorCS", {"start": v(-144.95, -161.61) * mm, "end": v(-145.14, -178.61) * mm});
            skLineSegment(sketch, "E86.MirrorCS", {"start": v(-152.95, -161.52) * mm, "end": v(-153.14, -178.52) * mm});
            skArc(sketch, "E87.MirrorCS", {"start": v(-152.95, -161.52) * mm, "mid": v(-148.9, -157.57) * mm, "end": v(-144.95, -161.61) * mm});
            skArc(sketch, "E88.MirrorCS", {"start": v(-151.66, 71.36) * mm, "mid": v(-147.66, 67.36) * mm, "end": v(-143.66, 71.36) * mm});
            skLineSegment(sketch, "E89.MirrorCS", {"start": v(-143.66, 71.36) * mm, "end": v(-143.66, 88.36) * mm});
            skArc(sketch, "E90.MirrorCS", {"start": v(-143.66, 88.36) * mm, "mid": v(-147.66, 92.36) * mm, "end": v(-151.66, 88.36) * mm});
            skLineSegment(sketch, "E91.MirrorCS", {"start": v(-151.66, 71.36) * mm, "end": v(-151.66, 88.36) * mm});
            skSolve(sketch);
        }
        {
            var Q0;
            Q0=makeQuery(id+"F15.imprint","IMPRINT",FACE,{"disambiguationData":[TD([[makeQuery(id+"F15.imprint","IMPRINT",EDGE,{"derivedFrom":sQuery(id+"F15.wireOp",EDGE,"E84.MirrorCS")}),-1.0]])]});
            var Q1;
            Q1=makeQuery(id+"F15.imprint","IMPRINT",FACE,{"disambiguationData":[TD([[makeQuery(id+"F15.imprint","IMPRINT",EDGE,{"derivedFrom":sQuery(id+"F15.wireOp",EDGE,"E75.left")}),1.0]])]});
            var Q2;
            Q2=makeQuery(id+"F15.imprint","IMPRINT",FACE,{"disambiguationData":[TD([[makeQuery(id+"F15.imprint","IMPRINT",EDGE,{"derivedFrom":sQuery(id+"F15.wireOp",EDGE,"E80.MirrorCS")}),-1.0]])]});
            var Q3;
            Q3=makeQuery(id+"F15.imprint","IMPRINT",FACE,{"disambiguationData":[TD([[makeQuery(id+"F15.imprint","IMPRINT",EDGE,{"derivedFrom":sQuery(id+"F15.wireOp",EDGE,"E88.MirrorCS")}),1.0]])]});
            extrude(context, id + "F16", {"entities" : qUnion([Q0, Q1, Q2, Q3]), "depth" : 1 * mm});
        }
        {
            var Q0;
            Q0=makeQuery(id+"F11.boolean.opBoolean","SPLIT",FACE,{"disambiguationData":[TD([makeQuery(id+"F3.opExtrude","SWEPT_FACE",FACE,{"disambiguationData":[OSD([sQuery(id+"F2.wireOp",EDGE,"E26.MirrorCS")])]})])],"derivedFrom":makeQuery(id+"F11.opExtrude","SWEPT_FACE",FACE,{"disambiguationData":[OSD([sQuery(id+"F10.wireOp",EDGE,"E66.MirrorCS")])]})});
            var sketch = newSketch(context, id + "F17", { "sketchPlane" : qUnion([Q0])});
            skLineSegment(sketch, "E92.bottom", {"start": v(138.22, -49.58) * mm, "end": v(148.22, -49.58) * mm});
            skLineSegment(sketch, "E92.top", {"start": v(138.22, -69.58) * mm, "end": v(148.22, -69.58) * mm});
            skLineSegment(sketch, "E92.left", {"start": v(138.22, -49.58) * mm, "end": v(138.22, -69.58) * mm});
            skLineSegment(sketch, "E92.right", {"start": v(148.22, -49.58) * mm, "end": v(148.22, -69.58) * mm});
            skPoint(sketch, "E93.endSnap0", {"position": v(143.22, -69.58) * mm});
            skLineSegment(sketch, "E94", {"start": v(141.72, -63.46) * mm, "end": v(144.72, -63.46) * mm, "construction": true});
            skLineSegment(sketch, "E95", {"start": v(143.22, -63.46) * mm, "end": v(143.22, -65.67) * mm, "construction": true});
            skLineSegment(sketch, "E96", {"start": v(145.22, -49.58) * mm, "end": v(145.22, -69.58) * mm});
            skLineSegment(sketch, "E97", {"start": v(141.22, -49.58) * mm, "end": v(141.22, -69.58) * mm});
            skSolve(sketch);
        }
        {
            var Q0;
            {var subQ0=sQuery(id+"F17.wireOp",EDGE,"E92.left");Q0=makeQuery(id+"F17.imprint","IMPRINT",FACE,{"disambiguationData":[TD([[makeQuery(id+"F17.imprint","IMPRINT",EDGE,{"derivedFrom":subQ0}),1.0]])]});}
            var Q1;
            Q1=makeQuery(id+"F11.boolean.opBoolean","SPLIT",FACE,{"disambiguationData":[TD([makeQuery(id+"F3.opExtrude","SWEPT_FACE",FACE,{"disambiguationData":[OSD([sQuery(id+"F2.wireOp",EDGE,"E26.MirrorCS")])]})])],"derivedFrom":makeQuery(id+"F11.opExtrude","SWEPT_FACE",FACE,{"disambiguationData":[OSD([sQuery(id+"F10.wireOp",EDGE,"E65.MirrorCS")])]})});
            extrude(context, id + "F18", {"entities" : qUnion([Q0]), "endBound" : BoundingType.UP_TO_SURFACE, "oppositeDirection" : true, "endBoundEntityFace" : qUnion([Q1]), "depth" : 25 * mm});
        }
        {
            var Q0;
            {var subQ0=sQuery(id+"F17.wireOp",EDGE,"E92.left");Q0=makeQuery(id+"F17.imprint","IMPRINT",FACE,{"disambiguationData":[TD([[makeQuery(id+"F17.imprint","IMPRINT",EDGE,{"derivedFrom":subQ0}),1.0]])]});}
            var Q1;
            {var subQ0=sQuery(id+"F0.wireOp",EDGE,"E17.0");var subQ1=sQuery(id+"F2.wireOp",EDGE,"E23.MirrorCS");var subQ2=sQuery(id+"F2.wireOp",EDGE,"E25.MirrorCS");var subQ3=sQuery(id+"F10.wireOp",EDGE,"E66.MirrorCS");var subQ4=sQuery(id+"F10.wireOp",EDGE,"E67.MirrorCS");var subQ5=makeQuery(id+"F3.opExtrude","SWEPT_FACE",FACE,{"disambiguationData":[OSD([sQuery(id+"F2.wireOp",EDGE,"E26.MirrorCS")])]});var subQ18=makeQuery(id+"F11.boolean.opBoolean","SPLIT",EDGE,{"disambiguationData":[TD([subQ5])],"derivedFrom":makeQuery(id+"F11.opExtrude","SWEPT_EDGE",EDGE,{"disambiguationData":[OSD([subQ0,subQ1,subQ2,subQ3,subQ4])]})});var subQ21=sQuery(id+"F17.wireOp",EDGE,"E92.bottom");var subQ22=makeQuery(id+"F17.imprint","INTERSECT",VERTEX,{"derivedFrom":[subQ18,subQ21]});Q1=makeQuery(id+"F17.imprint","IMPRINT",FACE,{"disambiguationData":[TD([[makeQuery(id+"F17.imprint","IMPRINT",EDGE,{"disambiguationData":[TD([[subQ22,-1.0]])],"derivedFrom":subQ21}),-1.0]])]});}
            var Q2;
            {var subQ12=sQuery(id+"F17.wireOp",EDGE,"E97");Q2=makeQuery(id+"F17.imprint","IMPRINT",FACE,{"disambiguationData":[TD([[makeQuery(id+"F17.imprint","IMPRINT",EDGE,{"derivedFrom":subQ12}),1.0]])]});}
            var Q3;
            {var subQ16=sQuery(id+"F17.wireOp",EDGE,"E96");Q3=makeQuery(id+"F17.imprint","IMPRINT",FACE,{"disambiguationData":[TD([[makeQuery(id+"F17.imprint","IMPRINT",EDGE,{"derivedFrom":subQ16}),-1.0]])]});}
            var Q4;
            {var subQ0=sQuery(id+"F17.wireOp",EDGE,"E92.right");Q4=makeQuery(id+"F17.imprint","IMPRINT",FACE,{"disambiguationData":[TD([[makeQuery(id+"F17.imprint","IMPRINT",EDGE,{"derivedFrom":subQ0}),-1.0]])]});}
            extrude(context, id + "F19", {"entities" : qUnion([Q0, Q1, Q2, Q3, Q4]), "operationType" : NewBodyOperationType.ADD, "depth" : 3 * mm});
        }
        {
            var Q0;
            {var subQ0=sQuery(id+"F17.wireOp",EDGE,"E92.right");Q0=makeQuery(id+"F17.imprint","IMPRINT",FACE,{"disambiguationData":[TD([[makeQuery(id+"F17.imprint","IMPRINT",EDGE,{"derivedFrom":subQ0}),-1.0]])]});}
            extrude(context, id + "F20", {"entities" : qUnion([Q0]), "operationType" : NewBodyOperationType.ADD, "oppositeDirection" : true, "depth" : 25 * mm});
        }
        {
            var Q0;
            {var subQ0=sQuery(id+"F17.wireOp",EDGE,"E92.right");Q0=makeQuery(id+"F20.boolean.opBoolean","MERGE",FACE,{"derivedFrom":[makeQuery(id+"F19.opExtrude","SWEPT_FACE",FACE,{"disambiguationData":[OSD([subQ0])]}),makeQuery(id+"F20.opExtrude","SWEPT_FACE",FACE,{"disambiguationData":[OSD([subQ0])]})]});}
            var sketch = newSketch(context, id + "F21", { "sketchPlane" : qUnion([Q0])});
            skLineSegment(sketch, "E98.bottom", {"start": v(-69.58, 11.33) * mm, "end": v(-49.58, 11.33) * mm});
            skLineSegment(sketch, "E98.top", {"start": v(-69.58, 14.33) * mm, "end": v(-49.58, 14.33) * mm});
            skLineSegment(sketch, "E98.left", {"start": v(-69.58, 11.33) * mm, "end": v(-69.58, 14.33) * mm});
            skLineSegment(sketch, "E98.right", {"start": v(-49.58, 11.33) * mm, "end": v(-49.58, 14.33) * mm});
            skSolve(sketch);
        }
        {
            var Q0;
            Q0=makeQuery(id+"F21.imprint","IMPRINT",FACE,{"disambiguationData":[TD([[makeQuery(id+"F21.imprint","IMPRINT",EDGE,{"derivedFrom":sQuery(id+"F21.wireOp",EDGE,"E98.bottom")}),-1.0]])]});
            extrude(context, id + "F22", {"entities" : qUnion([Q0]), "operationType" : NewBodyOperationType.ADD, "depth" : 10 * mm});
        }
        {
            var Q0;
            Q0=makeQuery(id+"F22.boolean.opBoolean","MERGE",FACE,{"derivedFrom":[makeQuery(id+"F20.opExtrude","CAP_FACE",FACE,{"disambiguationData":[OSD([sQuery(id+"F17.wireOp",EDGE,"E92.bottom"),sQuery(id+"F17.wireOp",EDGE,"E92.top"),sQuery(id+"F17.wireOp",EDGE,"E92.right"),sQuery(id+"F17.wireOp",EDGE,"E96")])],"isStart":false}),makeQuery(id+"F22.opExtrude","SWEPT_FACE",FACE,{"disambiguationData":[OSD([sQuery(id+"F21.wireOp",EDGE,"E98.bottom")])]})]});
            var sketch = newSketch(context, id + "F23", { "sketchPlane" : qUnion([Q0])});
            skLineSegment(sketch, "E99.bottom", {"start": v(158.22, 69.58) * mm, "end": v(161.22, 69.58) * mm});
            skLineSegment(sketch, "E99.top", {"start": v(158.22, 49.58) * mm, "end": v(161.22, 49.58) * mm});
            skLineSegment(sketch, "E99.left", {"start": v(158.22, 69.58) * mm, "end": v(158.22, 49.58) * mm});
            skLineSegment(sketch, "E99.right", {"start": v(161.22, 69.58) * mm, "end": v(161.22, 49.58) * mm});
            skSolve(sketch);
        }
        {
            var Q0;
            Q0=makeQuery(id+"F23.imprint","IMPRINT",FACE,{"disambiguationData":[TD([[makeQuery(id+"F23.imprint","IMPRINT",EDGE,{"derivedFrom":sQuery(id+"F23.wireOp",EDGE,"E99.bottom")}),-1.0]])]});
            extrude(context, id + "F24", {"entities" : qUnion([Q0]), "operationType" : NewBodyOperationType.ADD, "oppositeDirection" : true, "depth" : 15 * mm});
        }
        {
            var Q0;
            Q0=makeQuery(id+"F1.opExtrude","CAP_FACE",FACE,{"disambiguationData":[OSD([sQuery(id+"F0.wireOp",EDGE,"E0.top"),sQuery(id+"F0.wireOp",EDGE,"E0.left"),sQuery(id+"F0.wireOp",EDGE,"E0.right"),sQuery(id+"F0.wireOp",EDGE,"E1"),sQuery(id+"F0.wireOp",EDGE,"E2"),sQuery(id+"F0.wireOp",EDGE,"E3.0"),sQuery(id+"F0.wireOp",EDGE,"E4"),sQuery(id+"F0.wireOp",EDGE,"E5.0"),sQuery(id+"F0.wireOp",EDGE,"E6.0"),sQuery(id+"F0.wireOp",EDGE,"E7.0"),sQuery(id+"F0.wireOp",EDGE,"E8.0"),sQuery(id+"F0.wireOp",EDGE,"E9.0"),sQuery(id+"F0.wireOp",EDGE,"E10.0"),sQuery(id+"F0.wireOp",EDGE,"E11.0"),sQuery(id+"F0.wireOp",EDGE,"E12.0"),sQuery(id+"F0.wireOp",EDGE,"E13.0"),sQuery(id+"F0.wireOp",EDGE,"E16"),sQuery(id+"F0.wireOp",EDGE,"E17.0"),sQuery(id+"F0.wireOp",EDGE,"E18"),sQuery(id+"F0.wireOp",EDGE,"E19")])],"isStart":true});
            var sketch = newSketch(context, id + "F25", { "sketchPlane" : qUnion([Q0])});
            skLineSegment(sketch, "E100.bottom", {"start": v(-155.28, 84.35) * mm, "end": v(-152.28, 84.35) * mm});
            skLineSegment(sketch, "E100.left", {"start": v(-155.28, 84.35) * mm, "end": v(-155.28, 94.35) * mm});
            skLineSegment(sketch, "E100.right", {"start": v(-152.28, 84.35) * mm, "end": v(-152.28, 94.35) * mm});
            skLineSegment(sketch, "E100.top", {"start": v(-155.28, 94.35) * mm, "end": v(-152.28, 94.35) * mm});
            skSolve(sketch);
        }
        {
            var Q0;
            {var subQ7=sQuery(id+"F25.wireOp",EDGE,"E100.right");Q0=makeQuery(id+"F25.imprint","IMPRINT",FACE,{"disambiguationData":[TD([[makeQuery(id+"F25.imprint","IMPRINT",EDGE,{"derivedFrom":subQ7}),1.0]])]});}
            var Q1;
            {var subQ6=sQuery(id+"F25.wireOp",EDGE,"E100.left");Q1=makeQuery(id+"F25.imprint","IMPRINT",FACE,{"disambiguationData":[TD([[makeQuery(id+"F25.imprint","IMPRINT",EDGE,{"derivedFrom":subQ6}),-1.0]])]});}
            extrude(context, id + "F26", {"entities" : qUnion([Q0, Q1]), "depth" : 40 * mm, "hasSecondDirection" : true, "secondDirectionOppositeDirection" : true, "secondDirectionDepth" : 10 * mm});
        }
        {
            var Q0;
            Q0=makeQuery(id+"F26.opExtrude","SWEPT_FACE",FACE,{"disambiguationData":[OSD([sQuery(id+"F25.wireOp",EDGE,"E100.right")])]});
            var sketch = newSketch(context, id + "F27", { "sketchPlane" : qUnion([Q0])});
            skLineSegment(sketch, "E101.bottom", {"start": v(-94.35, -40) * mm, "end": v(-84.35, -40) * mm});
            skLineSegment(sketch, "E101.top", {"start": v(-94.35, -37) * mm, "end": v(-84.35, -37) * mm});
            skLineSegment(sketch, "E101.left", {"start": v(-94.35, -40) * mm, "end": v(-94.35, -37) * mm});
            skLineSegment(sketch, "E101.right", {"start": v(-84.35, -40) * mm, "end": v(-84.35, -37) * mm});
            skSolve(sketch);
        }
        {
            var Q0;
            Q0=makeQuery(id+"F27.imprint","IMPRINT",FACE,{"disambiguationData":[TD([[makeQuery(id+"F27.imprint","IMPRINT",EDGE,{"derivedFrom":sQuery(id+"F27.wireOp",EDGE,"E101.bottom")}),-1.0]])]});
            extrude(context, id + "F28", {"entities" : qUnion([Q0]), "operationType" : NewBodyOperationType.ADD, "depth" : 245 * mm});
        }
        {
            var Q0;
            Q0=makeQuery(id+"F28.opExtrude","SWEPT_FACE",FACE,{"disambiguationData":[OSD([sQuery(id+"F27.wireOp",EDGE,"E101.top")])]});
            var sketch = newSketch(context, id + "F29", { "sketchPlane" : qUnion([Q0])});
            skLineSegment(sketch, "E102.bottom", {"start": v(92.72, -94.35) * mm, "end": v(89.72, -94.35) * mm});
            skLineSegment(sketch, "E102.top", {"start": v(92.72, -84.35) * mm, "end": v(89.72, -84.35) * mm});
            skLineSegment(sketch, "E102.left", {"start": v(92.72, -94.35) * mm, "end": v(92.72, -84.35) * mm});
            skLineSegment(sketch, "E102.right", {"start": v(89.72, -94.35) * mm, "end": v(89.72, -84.35) * mm});
            skSolve(sketch);
        }
        {
            var Q0;
            Q0=makeQuery(id+"F29.imprint","IMPRINT",FACE,{"disambiguationData":[TD([[makeQuery(id+"F29.imprint","IMPRINT",EDGE,{"derivedFrom":sQuery(id+"F29.wireOp",EDGE,"E102.bottom")}),-1.0]])]});
            extrude(context, id + "F30", {"entities" : qUnion([Q0]), "operationType" : NewBodyOperationType.ADD, "depth" : 20 * mm});
        }
        {
            var Q0;
            Q0=makeQuery(id+"F24.opExtrude","CAP_EDGE",EDGE,{"disambiguationData":[OSD([sQuery(id+"F23.wireOp",EDGE,"E99.bottom")])],"isStart":false});
            var Q1;
            Q1=makeQuery(id+"F24.opExtrude","CAP_EDGE",EDGE,{"disambiguationData":[OSD([sQuery(id+"F23.wireOp",EDGE,"E99.top")])],"isStart":false});
            var Q2;
            Q2=makeQuery(id+"F24.opExtrude","CAP_EDGE",EDGE,{"disambiguationData":[OSD([sQuery(id+"F23.wireOp",EDGE,"E99.right")])],"isStart":true});
            var Q3;
            Q3=makeQuery(id+"F20.opExtrude","CAP_EDGE",EDGE,{"disambiguationData":[OSD([sQuery(id+"F17.wireOp",EDGE,"E96")])],"isStart":false});
            var Q4;
            Q4=makeQuery(id+"F19.opExtrude","CAP_EDGE",EDGE,{"disambiguationData":[OSD([sQuery(id+"F17.wireOp",EDGE,"E92.right")])],"isStart":false});
            var Q5;
            Q5=makeQuery(id+"F19.opExtrude","CAP_EDGE",EDGE,{"disambiguationData":[OSD([sQuery(id+"F17.wireOp",EDGE,"E92.left")])],"isStart":false});
            var Q6;
            Q6=makeQuery(id+"F18.opExtrude","CAP_EDGE",EDGE,{"disambiguationData":[OSD([sQuery(id+"F17.wireOp",EDGE,"E92.top")])],"isStart":false});
            var Q7;
            Q7=makeQuery(id+"F18.opExtrude","CAP_EDGE",EDGE,{"disambiguationData":[OSD([sQuery(id+"F17.wireOp",EDGE,"E92.bottom")])],"isStart":false});
            var Q8;
            Q8=makeQuery(id+"F26.opExtrude","CAP_EDGE",EDGE,{"disambiguationData":[OSD([sQuery(id+"F25.wireOp",EDGE,"E100.left")])],"isStart":false});
            var Q9;
            Q9=makeQuery(id+"F28.opExtrude","CAP_EDGE",EDGE,{"disambiguationData":[OSD([sQuery(id+"F27.wireOp",EDGE,"E101.bottom")])],"isStart":false});
            fillet(context, id + "F31", {"entities" : qUnion([Q0, Q1, Q2, Q3, Q4, Q5, Q6, Q7, Q8, Q9]), "radius" : 3 * mm, "tangentPropagation" : true, "allowEdgeOverflow" : false});
        }
        {
            var Q0;
            Q0=makeQuery(id+"F9.opExtrude","SWEPT_EDGE",EDGE,{"disambiguationData":[OSD([sQuery(id+"F8.wireOp",EDGE,"E51.top"),sQuery(id+"F8.wireOp",EDGE,"E51.right")])]});
            var Q1;
            Q1=makeQuery(id+"F9.opExtrude","SWEPT_EDGE",EDGE,{"disambiguationData":[OSD([sQuery(id+"F8.wireOp",EDGE,"E51.top"),sQuery(id+"F8.wireOp",EDGE,"E51.left")])]});
            var Q2;
            Q2=makeQuery(id+"F9.opExtrude","SWEPT_EDGE",EDGE,{"disambiguationData":[OSD([sQuery(id+"F8.wireOp",EDGE,"E52.MirrorCS"),sQuery(id+"F8.wireOp",EDGE,"E53.MirrorCS")])]});
            var Q3;
            Q3=makeQuery(id+"F9.opExtrude","SWEPT_EDGE",EDGE,{"disambiguationData":[OSD([sQuery(id+"F8.wireOp",EDGE,"E53.MirrorCS"),sQuery(id+"F8.wireOp",EDGE,"E54.MirrorCS")])]});
            var Q4;
            Q4=makeQuery(id+"F30.opExtrude","CAP_EDGE",EDGE,{"disambiguationData":[OSD([sQuery(id+"F29.wireOp",EDGE,"E102.bottom")])],"isStart":false});
            var Q5;
            Q5=makeQuery(id+"F30.opExtrude","CAP_EDGE",EDGE,{"disambiguationData":[OSD([sQuery(id+"F29.wireOp",EDGE,"E102.top")])],"isStart":false});
            fillet(context, id + "F32", {"entities" : qUnion([Q0, Q1, Q2, Q3, Q4, Q5]), "radius" : 3 * mm, "tangentPropagation" : true, "allowEdgeOverflow" : false});
        }
        {
            var Q0;
            Q0=makeQuery(id+"F30.boolean.opBoolean","MERGE",FACE,{"derivedFrom":[makeQuery(id+"F28.boolean.opBoolean","MERGE",FACE,{"derivedFrom":[makeQuery(id+"F26.opExtrude","SWEPT_FACE",FACE,{"disambiguationData":[OSD([sQuery(id+"F25.wireOp",EDGE,"E100.bottom")])]}),makeQuery(id+"F28.opExtrude","SWEPT_FACE",FACE,{"disambiguationData":[OSD([sQuery(id+"F27.wireOp",EDGE,"E101.right")])]})]}),makeQuery(id+"F30.opExtrude","SWEPT_FACE",FACE,{"disambiguationData":[OSD([sQuery(id+"F29.wireOp",EDGE,"E102.top")])]})]});
            cPlane(context, id + "F33", {"entities" : qUnion([Q0]), "cplaneType" : CPlaneType.OFFSET, "offset" : 130 * mm, "width" : 150 * mm, "height" : 150 * mm});
        }
        {
            var Q0;
            Q0=makeQuery(id+"F26.opExtrude","SWEPT_BODY",BODY,{"disambiguationData":[OSD([sQuery(id+"F25.wireOp",EDGE,"E100.bottom"),sQuery(id+"F25.wireOp",EDGE,"E100.left"),sQuery(id+"F25.wireOp",EDGE,"E100.right"),sQuery(id+"F25.wireOp",EDGE,"E100.top")])]});
            var Q1;
            Q1=qCreatedBy(id+"F33.planeOp",FACE);
            mirror(context, id + "F34", {"operationType" : NewBodyOperationType.ADD, "entities" : qUnion([Q0]), "mirrorPlane" : qUnion([Q1])});
        }
    });
